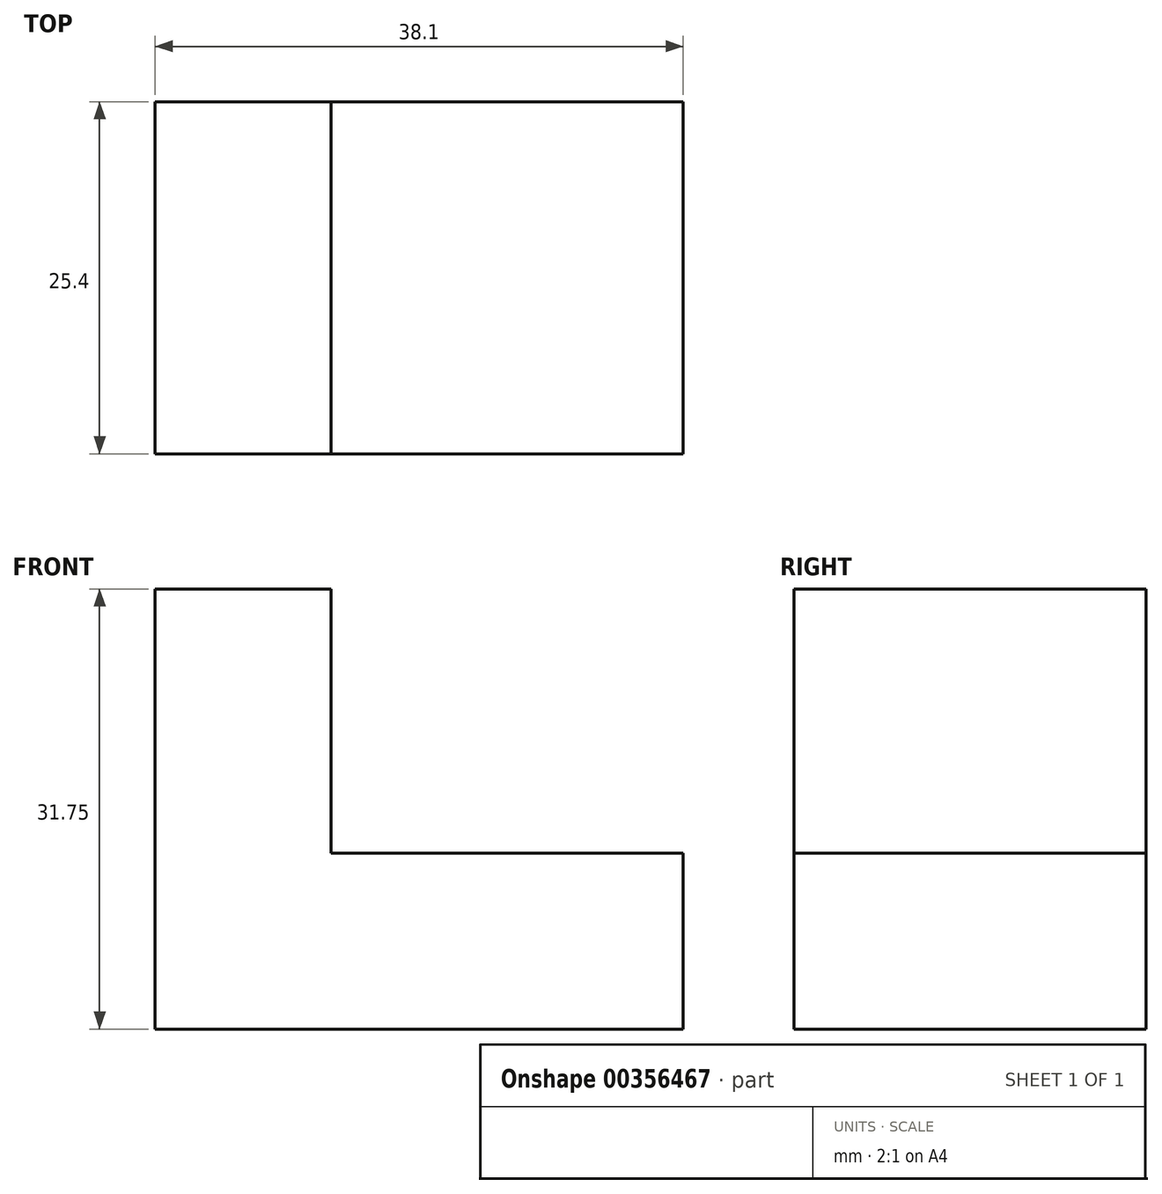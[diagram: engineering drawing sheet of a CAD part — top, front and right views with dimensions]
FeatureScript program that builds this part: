
annotation { "Feature Type Name" : "Feature", "Feature Type Description" : "" }
export const myFeature = defineFeature(function(context is Context, id is Id, definition is map)
    precondition{}
    {
        {
            var Q0;
            Q0=qCreatedBy(makeId("Front.planeOp"),FACE);
            var sketch = newSketch(context, id + "F0", { "sketchPlane" : qUnion([Q0])});
            skLineSegment(sketch, "E0", {"start": v(0, 0) * mm, "end": v(0, 31.75) * mm});
            skLineSegment(sketch, "E1", {"start": v(12.7, 31.75) * mm, "end": v(12.7, 12.7) * mm});
            skLineSegment(sketch, "E2", {"start": v(12.7, 12.7) * mm, "end": v(38.1, 12.7) * mm});
            skLineSegment(sketch, "E3", {"start": v(38.1, 12.7) * mm, "end": v(38.1, 0) * mm});
            skLineSegment(sketch, "E4", {"start": v(38.1, 0) * mm, "end": v(0, 0) * mm});
            skLineSegment(sketch, "E5", {"start": v(0, 31.75) * mm, "end": v(12.7, 31.75) * mm});
            skSolve(sketch);
        }
        {
            var Q0;
            Q0 = qSketchRegion(id + "F0", true);
            extrude(context, id + "F1", {"entities" : qUnion([Q0]), "depth" : 25.4 * mm});
        }
    });
